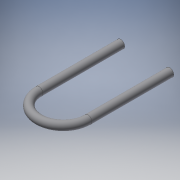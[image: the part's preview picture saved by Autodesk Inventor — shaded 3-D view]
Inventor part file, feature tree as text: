
AUTODESK INVENTOR PART (.ipt)
format: ipt  version: 2019 (Build 230136000, 136)  size: 124,928 bytes
history: native  units: mm
features: sketch x2, projected_geometry x2, revolve x1, extrude x1
ambient origin geometry x8: Origin, YZ Plane, XZ Plane, XY Plane, X Axis, Y Axis, Z Axis, Center Point
bodies: Body1 (feature_tree)
feature tree (6):
  revolve  "Revolution1"  [1 undecoded]
  extrude  "Extrusion1"  Depth=10.0mm TaperAngle=0.0deg
  sketch  "Sketch5"  dims[d8=1.0mm d9=3.0mm]
  sketch  "Sketch6"  dims[d10=180.0deg d11=10.0mm d12=0.0mm]
  projected_geometry  "Projected Loop1"
  projected_geometry  "Projected Loop2"
note: 1 required parameter value undecoded (feature->parameter linkage not recoverable at this tier; creation-order binding heuristic only, values carry confidence <= 0.55)
